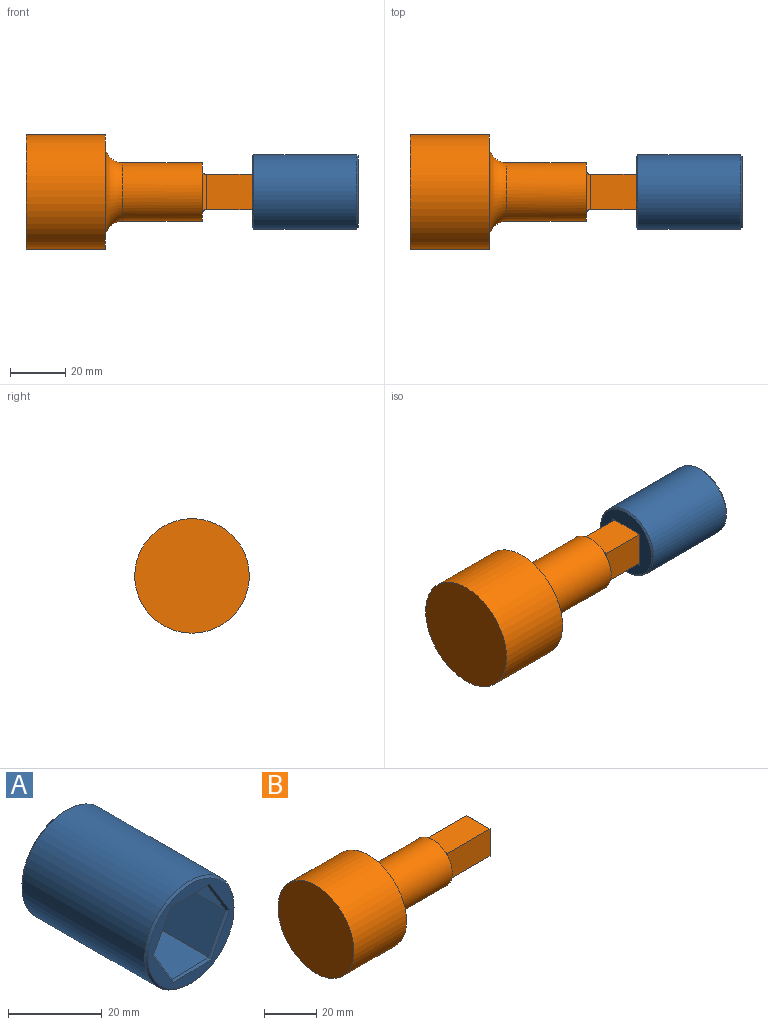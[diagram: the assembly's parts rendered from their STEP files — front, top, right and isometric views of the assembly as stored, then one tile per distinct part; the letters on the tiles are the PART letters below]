
ASSEMBLY  parts=2 mates=2
PART A: 26 faces, bbox 27x38.1x27 mm
  f0: plane 25.97x25.97mm, normal (0,1,0), area 341.6mm2, adj f14,f15,f16,f17,f18
  f1: plane 21.99x19.36mm, normal (0,-1,0), area 153mm2, adj f4,f5,f6,f7,f8,f9,f10,f11
  f2: cylinder r=13.49mm len=37.08mm, axis (0,1,0), area 3144.1mm2, adj f18,f25
  f3: plane 25.97x25.97mm, normal (0,-1,0), area 181.1mm2, adj f19,f20,f21,f22,f23,f24,f25
  f4: plane 23.3x10.99mm, normal (-0.03,0,1), area 256.3mm2, adj f1,f5,f9,f24
  f5: plane 23.3x9.68mm, normal (-0.88,0,0.47), area 256.3mm2, adj f1,f4,f6,f23
  f6: plane 23.3x9.36mm, normal (-0.85,0,-0.52), area 256.3mm2, adj f1,f5,f7,f21
  f7: plane 23.3x10.99mm, normal (0.03,0,-1), area 256.3mm2, adj f1,f6,f8,f19
  f8: plane 23.3x9.68mm, normal (0.88,0,-0.47), area 256.3mm2, adj f1,f7,f9,f20
  f9: plane 23.3x9.36mm, normal (0.85,0,0.52), area 256.3mm2, adj f1,f4,f8,f22
  f10: plane 13.78x12.7mm, normal (0,0,-1), area 175mm2, adj f1,f11,f13,f15
  f11: plane 13.78x12.7mm, normal (-1,0,0), area 175mm2, adj f1,f10,f12,f14
  f12: plane 13.78x12.7mm, normal (0,0,1), area 175mm2, adj f1,f11,f13,f16
  f13: plane 13.78x12.7mm, normal (1,0,0), area 175mm2, adj f1,f10,f12,f17
  f14: plane 13.72x0.51mm, normal (-0.71,0.71,0), area 9.5mm2, adj f0,f11,f15,f16
  f15: plane 13.72x0.51mm, normal (0,0.71,-0.71), area 9.5mm2, adj f0,f10,f14,f17
  f16: plane 13.72x0.51mm, normal (0,0.71,0.71), area 9.5mm2, adj f0,f12,f14,f17
  f17: plane 13.72x0.51mm, normal (0.71,0.71,0), area 9.5mm2, adj f0,f13,f15,f16
  f18: cone r=13.49mm half-angle=45deg, axis (0,-1,0), area 59.8mm2, adj f0,f2
  f19: plane 11.58x0.83mm, normal (0.02,-0.71,-0.71), area 8.1mm2, adj f3,f7,f20,f21
  f20: plane 10.2x5.81mm, normal (0.62,-0.71,-0.34), area 8.1mm2, adj f3,f8,f19,f22
  f21: plane 9.88x6.36mm, normal (-0.6,-0.71,-0.37), area 8.1mm2, adj f3,f6,f19,f23
  f22: plane 9.88x6.36mm, normal (0.6,-0.71,0.37), area 8.1mm2, adj f3,f9,f20,f24
  f23: plane 10.2x5.81mm, normal (-0.62,-0.71,0.34), area 8.1mm2, adj f3,f5,f21,f24
  f24: plane 11.58x0.83mm, normal (-0.02,-0.71,0.71), area 8.1mm2, adj f3,f4,f22,f23
  f25: cone r=12.99mm half-angle=45deg, axis (0,1,0), area 59.8mm2, adj f2,f3
PART B: 22 faces, bbox 88.9x46.2x46.2 mm
  f0: plane 13.68x2.54mm, normal (1,0,0), area 23.8mm2, adj f3,f17
  f1: plane 13.68x2.54mm, normal (1,0,0), area 23.8mm2, adj f3,f15
  f2: plane 13.68x2.54mm, normal (1,0,0), area 23.8mm2, adj f3,f14
  f3: cylinder r=10.48mm len=28.67mm, axis (1,0,0), area 1881.3mm2, adj f0,f1,f2,f7,f12,f14,f15,f16
  f4: plane 41.28x41.28mm, normal (1,0,0), area 448.4mm2, adj f5,f7
  f5: cylinder r=20.64mm len=41.28mm, axis (1,0,0), area 3705.3mm2, adj f4,f6
  f6: plane 41.28x41.28mm, normal (-1,0,0), area 1338mm2, adj f5
  f7: torus R=16.83mm, axis (1,0,0), area 801.3mm2, adj f3,f4
  f8: plane 23.05x12.7mm, normal (0,-1,0), area 292.7mm2, adj f9,f11,f14,f18
  f9: plane 23.05x12.7mm, normal (0,0,1), area 292.7mm2, adj f8,f10,f15,f19
  f10: plane 23.05x12.7mm, normal (0,1,0), area 292.7mm2, adj f9,f11,f17,f21
  f11: plane 23.05x12.7mm, normal (0,0,-1), area 292.7mm2, adj f8,f10,f16,f20
  f12: plane 13.68x2.54mm, normal (1,0,0), area 23.8mm2, adj f3,f16
  f13: plane 11.18x11.18mm, normal (1,0,0), area 124.9mm2, adj f18,f19,f20,f21
  f14: cylinder r=1.59mm len=14.82mm, axis (0,0,1), area 34mm2, adj f2,f3,f8,f15,f16
  f15: cylinder r=1.59mm len=14.82mm, axis (0,1,0), area 34mm2, adj f1,f3,f9,f14,f17
  f16: cylinder r=1.59mm len=14.82mm, axis (0,-1,0), area 34mm2, adj f3,f11,f12,f14,f17
  f17: cylinder r=1.59mm len=14.82mm, axis (0,0,-1), area 34mm2, adj f0,f3,f10,f15,f16
  f18: plane 12.7x0.76mm, normal (0.71,-0.71,0), area 12.9mm2, adj f8,f13,f19,f20
  f19: plane 12.7x0.76mm, normal (0.71,0,0.71), area 12.9mm2, adj f9,f13,f18,f21
  f20: plane 12.7x0.76mm, normal (0.71,0,-0.71), area 12.9mm2, adj f11,f13,f18,f21
  f21: plane 12.7x0.76mm, normal (0.71,0.71,0), area 12.9mm2, adj f10,f13,f19,f20
PLACE A rot(axis=(0,0,1),90deg) t=(71.67,13.98,-8.92)mm
PLACE B t=(-9.94,13.98,-8.92)mm fixed
MATE slider A.f2 <-> B.f3  axis (-1,0,0) through (72.18,13.98,-8.92)mm
MATE parallel A.f11 <-> B.f10  axis (0,-1,0) through (79.07,20.33,-8.92)mm
